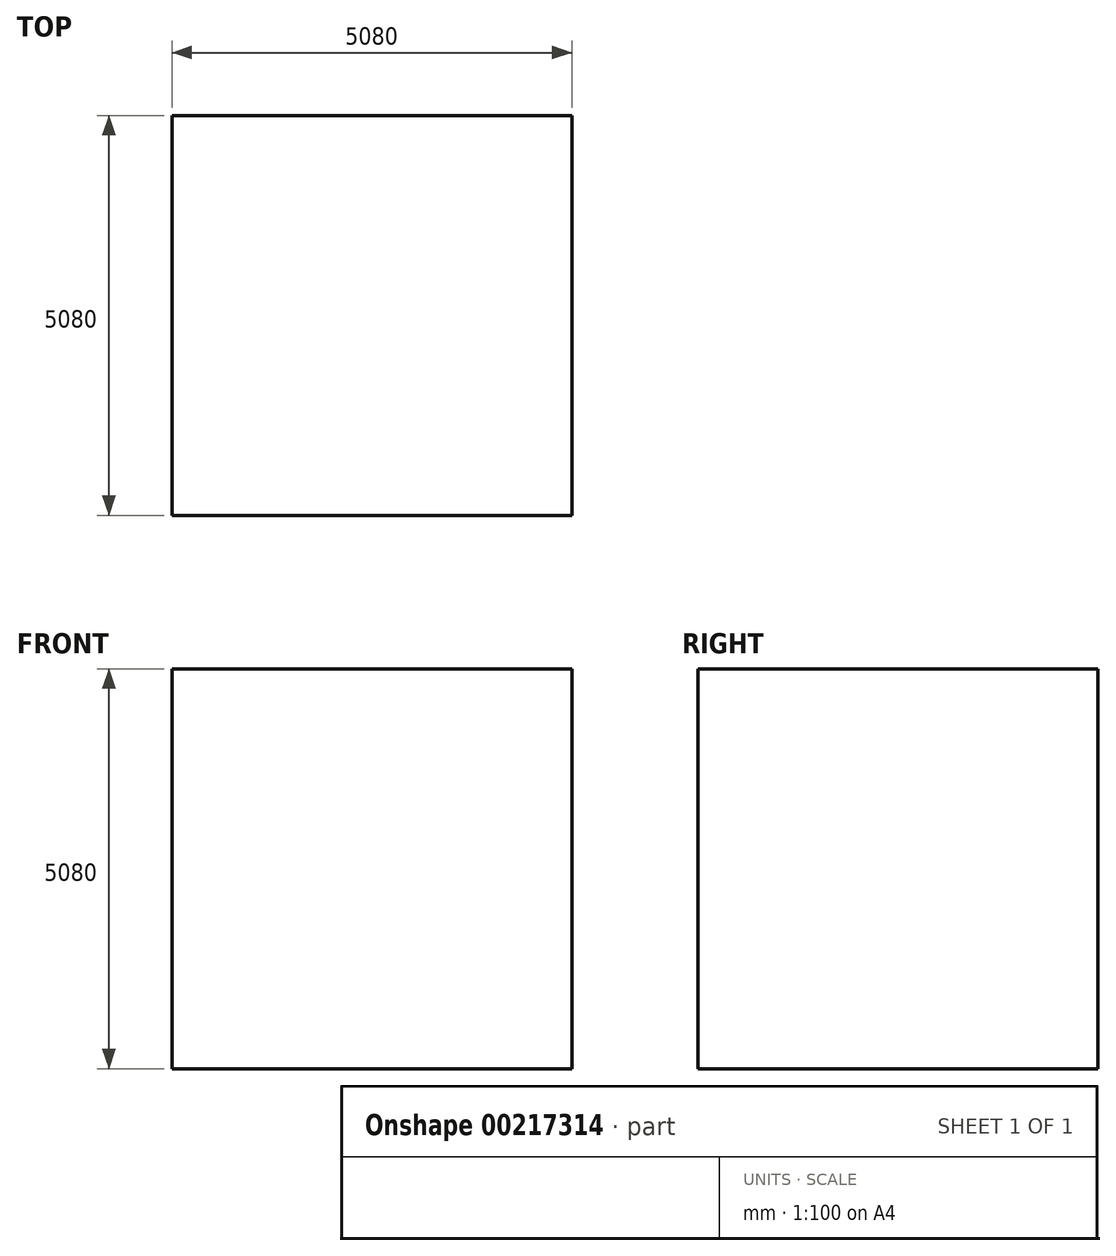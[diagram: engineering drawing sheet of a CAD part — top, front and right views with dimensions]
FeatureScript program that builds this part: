
annotation { "Feature Type Name" : "Feature", "Feature Type Description" : "" }
export const myFeature = defineFeature(function(context is Context, id is Id, definition is map)
    precondition{}
    {
        {
            var Q0;
            Q0=qCreatedBy(makeId("Top.planeOp"),FACE);
            var sketch = newSketch(context, id + "F0", { "sketchPlane" : qUnion([Q0])});
            skLineSegment(sketch, "E0.bottom", {"start": v(-5080, 5080) * mm, "end": v(0, 5080) * mm});
            skLineSegment(sketch, "E0.top", {"start": v(-5080, 0) * mm, "end": v(0, 0) * mm});
            skLineSegment(sketch, "E0.left", {"start": v(-5080, 5080) * mm, "end": v(-5080, 0) * mm});
            skLineSegment(sketch, "E0.right", {"start": v(0, 5080) * mm, "end": v(0, 0) * mm});
            skSolve(sketch);
        }
        {
            var Q0;
            Q0 = qSketchRegion(id + "F0", true);
            var Q1;
            Q1=sQuery(id+"F0.wireOp",EDGE,"E0.top");
            var Q2;
            Q2=sQuery(id+"F0.wireOp",EDGE,"E0.left");
            var Q3;
            Q3=sQuery(id+"F0.wireOp",EDGE,"E0.right");
            var Q4;
            Q4=sQuery(id+"F0.wireOp",EDGE,"E0.bottom");
            extrude(context, id + "F1", {"entities" : qUnion([Q0]), "bodyType" : ToolBodyType.SURFACE, "surfaceEntities" : qUnion([Q1, Q2, Q3, Q4]), "depth" : 5080 * mm});
        }
    });
